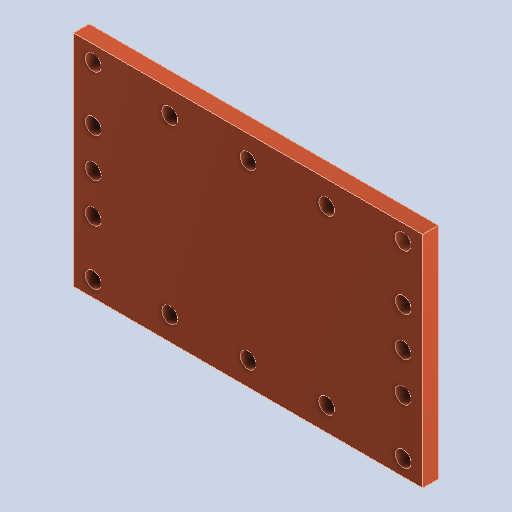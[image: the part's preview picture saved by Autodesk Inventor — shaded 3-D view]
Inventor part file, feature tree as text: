
AUTODESK INVENTOR PART (.ipt)
format: ipt  version: 2025.1 (Build 291241000, 241)  size: 140,800 bytes
history: native  units: mm
features: sketch x4, other x3, plane x1
ambient origin geometry x8: Origin, YZ Plane, XZ Plane, XY Plane, X Axis, Y Axis, Z Axis, Center Point
bodies: Volumenkörper1 (feature_tree)
feature tree (8):
  other  "1152.ipt"
  other  "Volumenkörper1::1152.ipt"
  other  "TaggingFeature1"
  sketch  "Skizze1"  dims[d0=10.0mm]
  sketch  "Skizze2"
  sketch  "Skizze3"
  sketch  "Skizze4"
  plane  "Arbeitsebene1"
